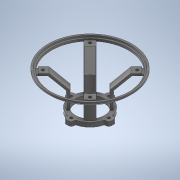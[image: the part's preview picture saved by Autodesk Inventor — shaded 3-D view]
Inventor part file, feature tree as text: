
AUTODESK INVENTOR PART (.ipt)
format: ipt  version: 2020 (Build 240168000, 168)  size: 470,528 bytes
history: native  units: mm
features: other x11, sketch x8, revolve x4, extrude x3, projected_geometry x3, pattern_circular x1, fillet x1
ambient origin geometry x8: Origin, YZ Plane, XZ Plane, XY Plane, X Axis, Y Axis, Z Axis, Center Point
bodies: Body1 (feature_tree)
feature tree (31):
  other  "Твердое тело1"
  extrude  "Выдавливание1"  Depth=34.0mm
  other  "РабПлоскость1"
  other  "РабОсь1"
  revolve  "Вращение1"
  sketch  "Эскиз3"
  other  "РабТочка1"
  extrude  "Выдавливание2"  Depth=45.0mm
  other  "РабТочка2"
  other  "РабТочка3"
  other  "РабТочка4"
  other  "РабПлоскость2"
  sketch  "Эскиз5"
  revolve  "Вращение2"
  revolve  "Вращение3"
  pattern_circular  "Круговой массив1"  Angle=45.0deg  [1 undecoded]
  extrude  "Выдавливание3"  Depth=3.3mm
  revolve  "Вращение4"
  sketch  "Эскиз8"
  fillet  "Сопряжение1"  Radius=9.0mm
  sketch  "Эскиз1"
  sketch  "Эскиз2"
  sketch  "Эскиз4"
  projected_geometry  "Спроецированная петля1"
  projected_geometry  "Спроецированная петля2"
  projected_geometry  "Спроецированная петля3"
  other  "РабПлоскость3"
  other  "РабПлоскость4"
  other  "РабПлоскость5"
  sketch  "Эскиз6"
  sketch  "Эскиз7"
note: 1 required parameter value undecoded (feature->parameter linkage not recoverable at this tier; creation-order binding heuristic only, values carry confidence <= 0.55)
